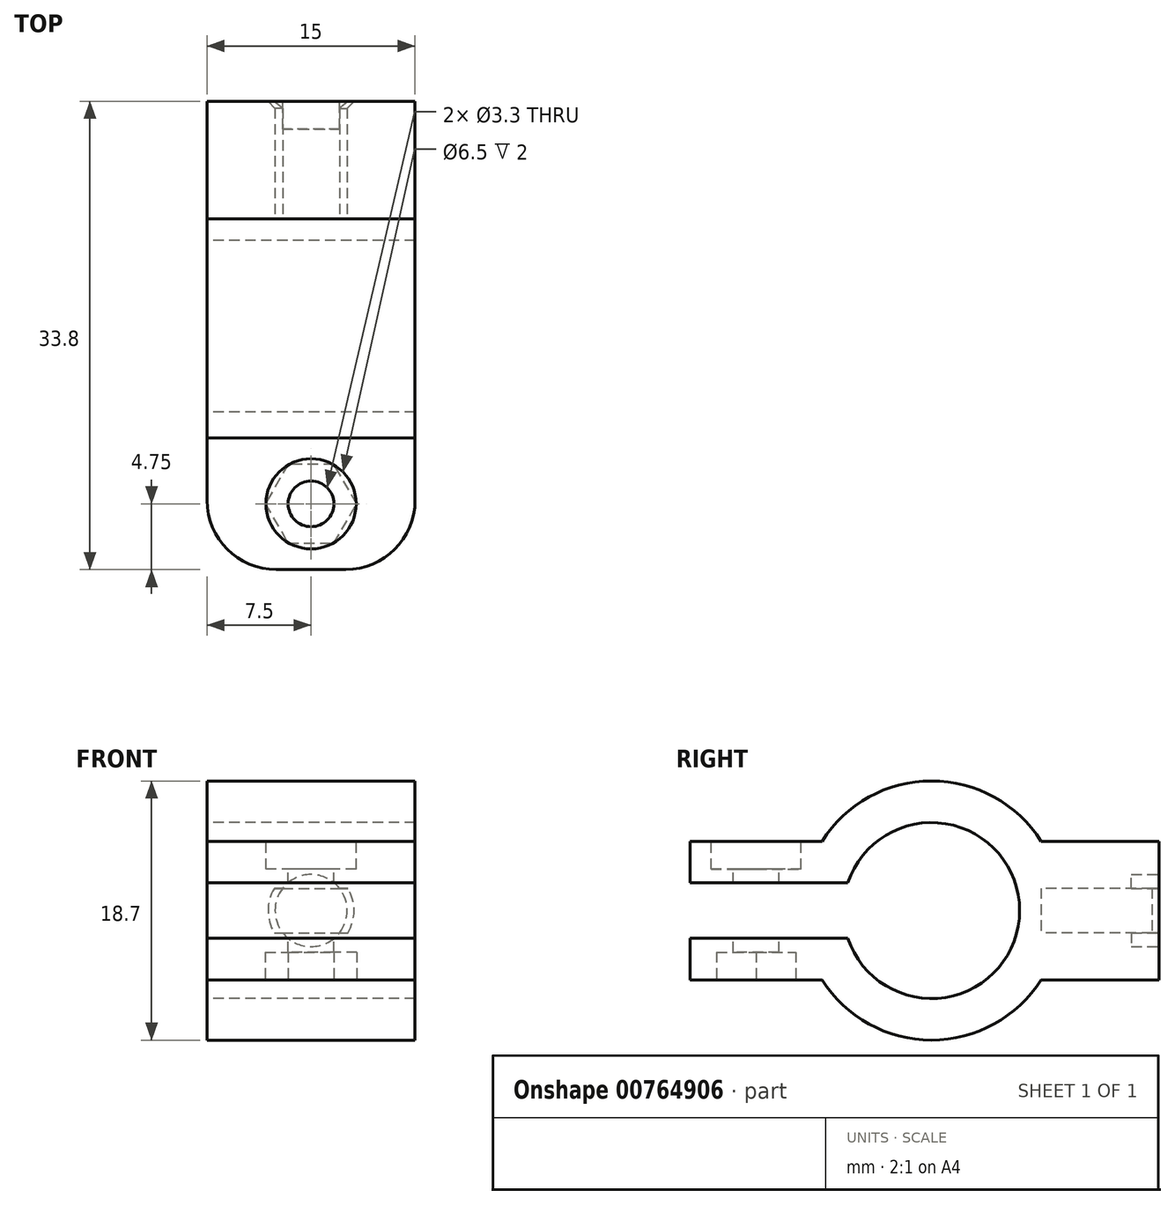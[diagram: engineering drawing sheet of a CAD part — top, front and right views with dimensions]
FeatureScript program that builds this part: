
annotation { "Feature Type Name" : "Feature", "Feature Type Description" : "" }
export const myFeature = defineFeature(function(context is Context, id is Id, definition is map)
    precondition{}
    {
        {
            var Q0;
            Q0=qCreatedBy(makeId("Front.planeOp"),FACE);
            var sketch = newSketch(context, id + "F0", { "sketchPlane" : qUnion([Q0])});
            skCircle(sketch, "E0", {"center": v(0, 0) * mm, "radius": 2.6 * mm, "construction": true});
            skLineSegment(sketch, "E1", {"start": v(-2.05, 1.6) * mm, "end": v(2.05, 1.6) * mm});
            skLineSegment(sketch, "E2", {"start": v(-2.05, -1.6) * mm, "end": v(2.05, -1.6) * mm});
            skArc(sketch, "E3", {"start": v(-2.05, 1.6) * mm, "mid": v(-2.6, 0) * mm, "end": v(-2.05, -1.6) * mm});
            skArc(sketch, "E4", {"start": v(2.05, -1.6) * mm, "mid": v(2.6, 0) * mm, "end": v(2.05, 1.6) * mm});
            skLineSegment(sketch, "E5.bottom", {"start": v(-7.5, -5) * mm, "end": v(7.5, -5) * mm});
            skLineSegment(sketch, "E5.top", {"start": v(-7.5, 5) * mm, "end": v(7.5, 5) * mm});
            skLineSegment(sketch, "E5.left", {"start": v(-7.5, -5) * mm, "end": v(-7.5, 5) * mm});
            skLineSegment(sketch, "E5.right", {"start": v(7.5, -5) * mm, "end": v(7.5, 5) * mm});
            skSolve(sketch);
        }
        {
            var Q0;
            Q0=makeQuery(id+"F0.imprint","IMPRINT",FACE,{"disambiguationData":[TD([[makeQuery(id+"F0.imprint","IMPRINT",EDGE,{"derivedFrom":sQuery(id+"F0.wireOp",EDGE,"E1")}),1.0]])]});
            extrude(context, id + "F1", {"entities" : qUnion([Q0]), "oppositeDirection" : true, "depth" : 8.5 * mm, "offsetDistance" : 25 * mm});
        }
        {
            var Q0;
            Q0=qCreatedBy(makeId("Right.planeOp"),FACE);
            var sketch = newSketch(context, id + "F2", { "sketchPlane" : qUnion([Q0])});
            skArc(sketch, "E6", {"start": v(-13.93, -2) * mm, "mid": v(-1.55, 0) * mm, "end": v(-13.93, 2) * mm});
            skArc(sketch, "E7", {"start": v(0, 5) * mm, "mid": v(-7.9, 9.35) * mm, "end": v(-15.8, 5) * mm});
            skLineSegment(sketch, "E8", {"start": v(-15.8, 5) * mm, "end": v(-25.3, 5) * mm});
            skLineSegment(sketch, "E9", {"start": v(-25.3, 5) * mm, "end": v(-25.3, 2) * mm});
            skLineSegment(sketch, "E10", {"start": v(-25.3, 2) * mm, "end": v(-13.93, 2) * mm});
            skArc(sketch, "E11", {"start": v(-15.8, -5) * mm, "mid": v(-7.9, -9.35) * mm, "end": v(0, -5) * mm});
            skLineSegment(sketch, "E12", {"start": v(-13.93, -2) * mm, "end": v(-25.3, -2) * mm});
            skLineSegment(sketch, "E13", {"start": v(-25.3, -2) * mm, "end": v(-25.3, -5) * mm});
            skLineSegment(sketch, "E14", {"start": v(-25.3, -5) * mm, "end": v(-15.8, -5) * mm});
            skLineSegment(sketch, "E15", {"start": v(0, 5) * mm, "end": v(0, -5) * mm});
            skSolve(sketch);
        }
        {
            var Q0;
            Q0 = qSketchRegion(id + "F2", true);
            extrude(context, id + "F3", {"entities" : qUnion([Q0]), "operationType" : NewBodyOperationType.ADD, "endBound" : BoundingType.SYMMETRIC, "depth" : 15 * mm, "offsetDistance" : 25 * mm});
        }
        {
            var Q0;
            Q0=makeQuery(id+"F3.opExtrude","SWEPT_FACE",FACE,{"disambiguationData":[OSD([sQuery(id+"F2.wireOp",EDGE,"E8")])]});
            var sketch = newSketch(context, id + "F4", { "sketchPlane" : qUnion([Q0])});
            skPoint(sketch, "E16", {"position": v(0, -20.55) * mm});
            skSolve(sketch);
        }
        {
            var Q0;
            Q0=sQuery(id+"F4.wireOp",VERTEX,"E16");
            var Q1;
            Q1=makeQuery(id+"F1.opExtrude","SWEPT_BODY",BODY,{"disambiguationData":[OSD([sQuery(id+"F0.wireOp",EDGE,"E1"),sQuery(id+"F0.wireOp",EDGE,"E2"),sQuery(id+"F0.wireOp",EDGE,"E3"),sQuery(id+"F0.wireOp",EDGE,"E4"),sQuery(id+"F0.wireOp",EDGE,"E5.bottom"),sQuery(id+"F0.wireOp",EDGE,"E5.top"),sQuery(id+"F0.wireOp",EDGE,"E5.left"),sQuery(id+"F0.wireOp",EDGE,"E5.right")])]});
            hole(context, id + "F5", {"style" : HoleStyle.C_BORE, "endStyle" : HoleEndStyle.THROUGH, "holeDiameter" : 3.3 * mm, "cBoreDiameter" : 6.5 * mm, "cBoreDepth" : 2 * mm, "majorDiameter" : 5 * mm, "isTappedThrough" : true, "tappedDepth" : 12 * mm, "tapClearance" : 3, "locations" : qUnion([Q0]), "scope" : qUnion([Q1])});
        }
        {
            var Q0;
            Q0=makeQuery(id+"F3.opExtrude","SWEPT_FACE",FACE,{"disambiguationData":[OSD([sQuery(id+"F2.wireOp",EDGE,"E14")])]});
            var sketch = newSketch(context, id + "F6", { "sketchPlane" : qUnion([Q0])});
            skCircle(sketch, "E17.cCircle", {"center": v(0, 20.55) * mm, "radius": 2.85 * mm, "construction": true});
            skLineSegment(sketch, "E17.0", {"start": v(1.65, 17.7) * mm, "end": v(-1.65, 17.7) * mm});
            skLineSegment(sketch, "E17.1", {"start": v(-1.65, 17.7) * mm, "end": v(-3.3, 20.55) * mm});
            skLineSegment(sketch, "E17.2", {"start": v(-3.3, 20.55) * mm, "end": v(-1.65, 23.4) * mm});
            skLineSegment(sketch, "E17.3", {"start": v(-1.65, 23.4) * mm, "end": v(1.65, 23.4) * mm});
            skLineSegment(sketch, "E17.4", {"start": v(1.65, 23.4) * mm, "end": v(3.3, 20.55) * mm});
            skLineSegment(sketch, "E17.5", {"start": v(3.3, 20.55) * mm, "end": v(1.65, 17.7) * mm});
            skPoint(sketch, "E17.0.midPoint", {"position": v(0, 17.7) * mm});
            skSolve(sketch);
        }
        {
            var Q0;
            Q0 = qSketchRegion(id + "F6", true);
            extrude(context, id + "F7", {"entities" : qUnion([Q0]), "operationType" : NewBodyOperationType.REMOVE, "oppositeDirection" : true, "depth" : 2 * mm, "offsetDistance" : 25 * mm});
        }
        {
            var Q0;
            Q0=makeQuery(id+"F3.opExtrude","CAP_EDGE",EDGE,{"disambiguationData":[OSD([sQuery(id+"F2.wireOp",EDGE,"E9")])],"isStart":false});
            var Q1;
            Q1=makeQuery(id+"F3.opExtrude","CAP_EDGE",EDGE,{"disambiguationData":[OSD([sQuery(id+"F2.wireOp",EDGE,"E9")])],"isStart":true});
            var Q2;
            Q2=makeQuery(id+"F3.opExtrude","CAP_EDGE",EDGE,{"disambiguationData":[OSD([sQuery(id+"F2.wireOp",EDGE,"E13")])],"isStart":true});
            var Q3;
            Q3=makeQuery(id+"F3.opExtrude","CAP_EDGE",EDGE,{"disambiguationData":[OSD([sQuery(id+"F2.wireOp",EDGE,"E13")])],"isStart":false});
            fillet(context, id + "F8", {"entities" : qUnion([Q0, Q1, Q2, Q3]), "radius" : 5 * mm, "tangentPropagation" : true, "allowEdgeOverflow" : false});
        }
        {
            var Q0;
            Q0=makeQuery(id+"F1.opExtrude","CAP_FACE",FACE,{"disambiguationData":[OSD([sQuery(id+"F0.wireOp",EDGE,"E1"),sQuery(id+"F0.wireOp",EDGE,"E2"),sQuery(id+"F0.wireOp",EDGE,"E3"),sQuery(id+"F0.wireOp",EDGE,"E4"),sQuery(id+"F0.wireOp",EDGE,"E5.bottom"),sQuery(id+"F0.wireOp",EDGE,"E5.top"),sQuery(id+"F0.wireOp",EDGE,"E5.left"),sQuery(id+"F0.wireOp",EDGE,"E5.right")])],"isStart":false});
            var sketch = newSketch(context, id + "F9", { "sketchPlane" : qUnion([Q0])});
            skCircle(sketch, "E18", {"center": v(0, 0) * mm, "radius": 2.6 * mm});
            skSolve(sketch);
        }
        {
            var Q0;
            {var subQ1=makeQuery(id+"F1.opExtrude","CAP_EDGE",EDGE,{"disambiguationData":[OSD([sQuery(id+"F0.wireOp",EDGE,"E1")])],"isStart":false});Q0=makeQuery(id+"F9.imprint","IMPRINT",FACE,{"disambiguationData":[TD([[makeQuery(id+"F9.imprint","IMPRINT",EDGE,{"derivedFrom":subQ1}),-1.0]])]});}
            var Q1;
            {var subQ1=makeQuery(id+"F1.opExtrude","CAP_EDGE",EDGE,{"disambiguationData":[OSD([sQuery(id+"F0.wireOp",EDGE,"E2")])],"isStart":false});Q1=makeQuery(id+"F9.imprint","IMPRINT",FACE,{"disambiguationData":[TD([[makeQuery(id+"F9.imprint","IMPRINT",EDGE,{"derivedFrom":subQ1}),1.0]])]});}
            extrude(context, id + "F10", {"entities" : qUnion([Q0, Q1]), "operationType" : NewBodyOperationType.REMOVE, "oppositeDirection" : true, "depth" : 2 * mm, "offsetDistance" : 25 * mm});
        }
        {
            var Q0;
            Q0=makeQuery(id+"F10.boolean.opBoolean","COPY",EDGE,{"derivedFrom":makeQuery(id+"F10.opExtrude","CAP_EDGE",EDGE,{"disambiguationData":[OSD([sQuery(id+"F0.wireOp",EDGE,"E1")])],"isStart":false})});
            var Q1;
            Q1=makeQuery(id+"F10.boolean.opBoolean","COPY",EDGE,{"derivedFrom":makeQuery(id+"F10.opExtrude","CAP_EDGE",EDGE,{"disambiguationData":[OSD([sQuery(id+"F0.wireOp",EDGE,"E2")])],"isStart":false})});
            var Q2;
            {var subQ0=sQuery(id+"F9.wireOp",EDGE,"E18");var subQ1=makeQuery(id+"F1.opExtrude","CAP_EDGE",EDGE,{"disambiguationData":[OSD([sQuery(id+"F0.wireOp",EDGE,"E2")])],"isStart":false});var subQ2=makeQuery(id+"F1.opExtrude","CAP_EDGE",EDGE,{"disambiguationData":[OSD([sQuery(id+"F0.wireOp",EDGE,"E1")])],"isStart":false});Q2=makeQuery(id+"F10.boolean.opBoolean","MERGE",EDGE,{"derivedFrom":[makeQuery(id+"F1.opExtrude","CAP_EDGE",EDGE,{"disambiguationData":[OSD([sQuery(id+"F0.wireOp",EDGE,"E3")])],"isStart":false}),makeQuery(id+"F1.opExtrude","CAP_EDGE",EDGE,{"disambiguationData":[OSD([sQuery(id+"F0.wireOp",EDGE,"E4")])],"isStart":false}),makeQuery(id+"F10.opExtrude","CAP_EDGE",EDGE,{"disambiguationData":[OSD([subQ0]),TDD([makeQuery(id+"F9.imprint","IMPRINT",EDGE,{"disambiguationData":[TD([[makeQuery(id+"F9.imprint","INTERSECT",VERTEX,{"disambiguationData":[OD(0.0)],"derivedFrom":[subQ2,subQ0]}),-1.0],[makeQuery(id+"F9.imprint","INTERSECT",VERTEX,{"disambiguationData":[OD(1.0)],"derivedFrom":[subQ2,subQ0]}),1.0]])],"derivedFrom":subQ0})])],"isStart":true}),makeQuery(id+"F10.opExtrude","CAP_EDGE",EDGE,{"disambiguationData":[OSD([subQ0]),TDD([makeQuery(id+"F9.imprint","IMPRINT",EDGE,{"disambiguationData":[TD([[makeQuery(id+"F9.imprint","INTERSECT",VERTEX,{"disambiguationData":[OD(0.0)],"derivedFrom":[subQ1,subQ0]}),1.0],[makeQuery(id+"F9.imprint","INTERSECT",VERTEX,{"disambiguationData":[OD(1.0)],"derivedFrom":[subQ1,subQ0]}),-1.0]])],"derivedFrom":subQ0})])],"isStart":true})]});}
            chamfer(context, id + "F11", {"entities" : qUnion([Q0, Q1, Q2]), "width" : 0.5 * mm, "tangentPropagation" : true});
        }
    });
